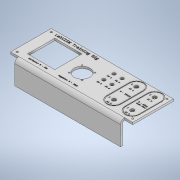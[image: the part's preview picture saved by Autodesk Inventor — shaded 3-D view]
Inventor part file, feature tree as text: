
AUTODESK INVENTOR PART (.ipt)
format: ipt  version: 2022 (Build 260153000, 153)  size: 2,321,920 bytes
history: native  units: in
note: dims shown in document units (in); Inventor stores cm internally (conversion verified against a paired STEP export)
features: sketch x6, extrude x5, other x1
ambient origin geometry x8: Origin, YZ Plane, XZ Plane, XY Plane, X Axis, Y Axis, Z Axis, Center Point
bodies: Solid1 (feature_tree)
feature tree (12):
  extrude  "Extrusion1"  Depth=2.1654in
  extrude  "Extrusion2"  Depth=0.7874in
  extrude  "Extrusion3"  Depth=5.9055in
  extrude  "Extrusion4"  Depth=0.1969in TaperAngle=0.0deg
  extrude  "Extrusion5"  Depth=2.6378in
  other  "Bend Part3"
  sketch  "Sketch1"  dims[d0=3.937in d1=2.1654in]
  sketch  "Sketch2"  dims[d2=11.811in d3=0.7874in]
  sketch  "Sketch3"  dims[d4=0.7874in d5=5.9055in]
  sketch  "Sketch4"  dims[d6=1.9685in d7=0.1969in d8=0.0in]
  sketch  "Sketch5"  dims[d11=2.6378in d12=2.6378in]
  sketch  "Sketch6"  dims[d13=0.6496in d15=0.9843in d16=1.5354in d17=1.5748in d18=1.5748in d19=1.2598in d20=1.2598in d23=0.6299in d24=0.6299in d25=0.1181in d26=0.1181in d27=0.1181in d28=0.1181in d29=0.374in d30=1.7717in d31=2.1654in d32=0.7874in d34=0.315in d36=0.7874in d37=0.9843in d38=0.7874in d39=1.6535in d40=1.378in d41=0.4331in d42=0.1024in d43=0.0512in d44=0.1024in d45=0.0512in d46=0.1024in d47=0.0512in d48=0.1024in d49=0.0512in d50=0.4331in d51=0.0in d52=0.0in d55=0.1772in d58=0.315in d59=0.315in d60=0.315in d62=0.315in d63=0.3937in d64=0.0in d65=0.6496in d66=0.3937in d67=0.3937in d68=0.1969in d69=0.1969in d70=0.3937in d71=0.2362in d72=0.2362in d73=0.3937in d74=1.063in d75=0.4331in d76=0.4331in d77=0.4331in d79=0.4331in d80=0.3937in d81=0.3937in d82=0.9055in d83=0.9055in d84=0.1575in d85=0.3937in d86=0.0in d87=0.1969in d88=90.0deg d89=1.2598in d90=1.2598in d92=0.0787in d93=0.0787in d94=0.0394in d95=0.0in]
